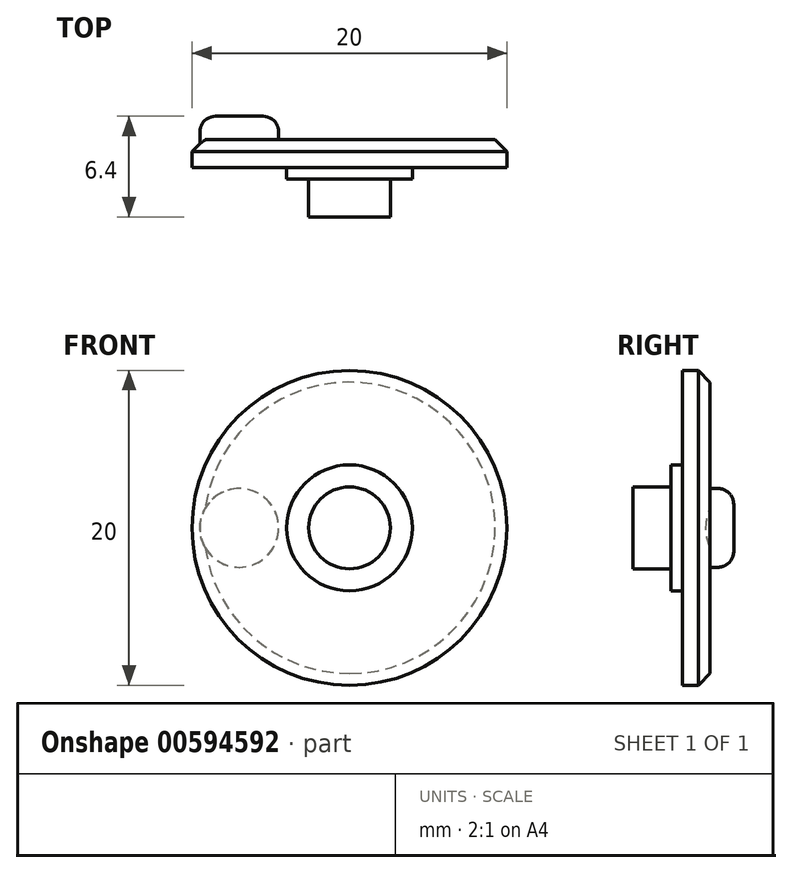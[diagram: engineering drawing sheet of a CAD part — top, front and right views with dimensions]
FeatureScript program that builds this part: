
annotation { "Feature Type Name" : "Feature", "Feature Type Description" : "" }
export const myFeature = defineFeature(function(context is Context, id is Id, definition is map)
    precondition{}
    {
        {
            var Q0;
            Q0=qCreatedBy(makeId("Top.planeOp"),FACE);
            var sketch = newSketch(context, id + "F0", { "sketchPlane" : qUnion([Q0])});
            skLineSegment(sketch, "E0", {"start": v(0, -4.9) * mm, "end": v(2.6, -4.9) * mm});
            skLineSegment(sketch, "E1", {"start": v(2.6, -4.9) * mm, "end": v(2.6, -2.8) * mm});
            skLineSegment(sketch, "E2", {"start": v(2.6, -2.5) * mm, "end": v(4, -2.5) * mm});
            skLineSegment(sketch, "E3", {"start": v(4, -2.5) * mm, "end": v(4, -1.75) * mm});
            skLineSegment(sketch, "E4", {"start": v(4, -1.75) * mm, "end": v(10, -1.75) * mm});
            skLineSegment(sketch, "E5", {"start": v(10, -1.75) * mm, "end": v(10, 0) * mm});
            skLineSegment(sketch, "E6", {"start": v(10, 0) * mm, "end": v(0, 0) * mm});
            skLineSegment(sketch, "E7", {"start": v(0, 0) * mm, "end": v(0, -4.9) * mm});
            skLineSegment(sketch, "E8", {"start": v(2.6, -2.8) * mm, "end": v(2.6, -2.5) * mm});
            skSolve(sketch);
        }
        {
            var Q0;
            Q0=makeQuery(id+"F0.imprint","IMPRINT",FACE,{"disambiguationData":[TD([[makeQuery(id+"F0.imprint","IMPRINT",EDGE,{"derivedFrom":sQuery(id+"F0.wireOp",EDGE,"E0")}),1.0]])]});
            var Q1;
            Q1=sQuery(id+"F0.wireOp",EDGE,"E7");
            revolve(context, id + "F1", {"entities" : qUnion([Q0]), "axis" : qUnion([Q1]), "revolveType" : RevolveType.FULL});
        }
        {
            var Q0;
            Q0=makeQuery(id+"F1.opRevolve","SWEPT_FACE",FACE,{"disambiguationData":[OSD([sQuery(id+"F0.wireOp",EDGE,"E6")])]});
            var sketch = newSketch(context, id + "F2", { "sketchPlane" : qUnion([Q0])});
            skLineSegment(sketch, "E9", {"start": v(0, 0) * mm, "end": v(18.21, 0) * mm, "construction": true});
            skCircle(sketch, "E10", {"center": v(7, 0) * mm, "radius": 2.5 * mm});
            skSolve(sketch);
        }
        {
            var Q0;
            {var subQ0=sQuery(id+"F2.wireOp",EDGE,"E10");var subQ1=sQuery(id+"F0.wireOp",EDGE,"E6");var subQ2=makeQuery(id+"F5.opChamfer","BLEND_EDGE",EDGE,{"blendedFrom":[makeQuery(id+"F1.opRevolve","SWEPT_EDGE",EDGE,{"disambiguationData":[OSD([sQuery(id+"F0.wireOp",EDGE,"E5"),subQ1])]}),makeQuery(id+"F1.opRevolve","SWEPT_FACE",FACE,{"disambiguationData":[OSD([subQ1])]})],"blendedInto":[makeQuery(id+"F1.opRevolve","SWEPT_FACE",FACE,{"disambiguationData":[OSD([subQ1])]})]});var subQ3=makeQuery(id+"F2.imprint","INTERSECT",VERTEX,{"disambiguationData":[OD(0.0)],"derivedFrom":[subQ2,subQ0]});Q0=makeQuery(id+"F2.imprint","IMPRINT",FACE,{"disambiguationData":[TD([[makeQuery(id+"F2.imprint","IMPRINT",EDGE,{"disambiguationData":[TD([[subQ3,1.0]])],"derivedFrom":subQ0}),1.0]])]});}
            var Q1;
            {var subQ0=sQuery(id+"F2.wireOp",EDGE,"E10");var subQ1=sQuery(id+"F0.wireOp",EDGE,"E6");var subQ2=makeQuery(id+"F5.opChamfer","BLEND_EDGE",EDGE,{"blendedFrom":[makeQuery(id+"F1.opRevolve","SWEPT_EDGE",EDGE,{"disambiguationData":[OSD([sQuery(id+"F0.wireOp",EDGE,"E5"),subQ1])]}),makeQuery(id+"F1.opRevolve","SWEPT_FACE",FACE,{"disambiguationData":[OSD([subQ1])]})],"blendedInto":[makeQuery(id+"F1.opRevolve","SWEPT_FACE",FACE,{"disambiguationData":[OSD([subQ1])]})]});var subQ3=makeQuery(id+"F2.imprint","INTERSECT",VERTEX,{"disambiguationData":[OD(0.0)],"derivedFrom":[subQ2,subQ0]});Q1=makeQuery(id+"F2.imprint","IMPRINT",FACE,{"disambiguationData":[TD([[makeQuery(id+"F2.imprint","IMPRINT",EDGE,{"disambiguationData":[TD([[subQ3,-1.0]])],"derivedFrom":subQ0}),1.0]])]});}
            var Q2;
            Q2=makeQuery(id+"F2.imprint","IMPRINT",FACE,{"disambiguationData":[TD([[makeQuery(id+"F2.imprint","IMPRINT",EDGE,{"derivedFrom":sQuery(id+"F2.wireOp",EDGE,"E10")}),1.0]])]});
            extrude(context, id + "F3", {"entities" : qUnion([Q0, Q1, Q2]), "operationType" : NewBodyOperationType.ADD, "depth" : 1.5 * mm, "offsetDistance" : 25 * mm});
        }
        {
            var Q0;
            Q0=makeQuery(id+"F3.opExtrude","CAP_EDGE",EDGE,{"disambiguationData":[OSD([sQuery(id+"F2.wireOp",EDGE,"E10")])],"isStart":false});
            fillet(context, id + "F4", {"entities" : qUnion([Q0]), "radius" : 1 * mm, "tangentPropagation" : true, "allowEdgeOverflow" : false});
        }
        {
            var Q0;
            Q0=makeQuery(id+"F1.opRevolve","SWEPT_EDGE",EDGE,{"disambiguationData":[OSD([sQuery(id+"F0.wireOp",EDGE,"E5"),sQuery(id+"F0.wireOp",EDGE,"E6")])]});
            chamfer(context, id + "F5", {"entities" : qUnion([Q0]), "width" : 0.75 * mm, "tangentPropagation" : true});
        }
    });
